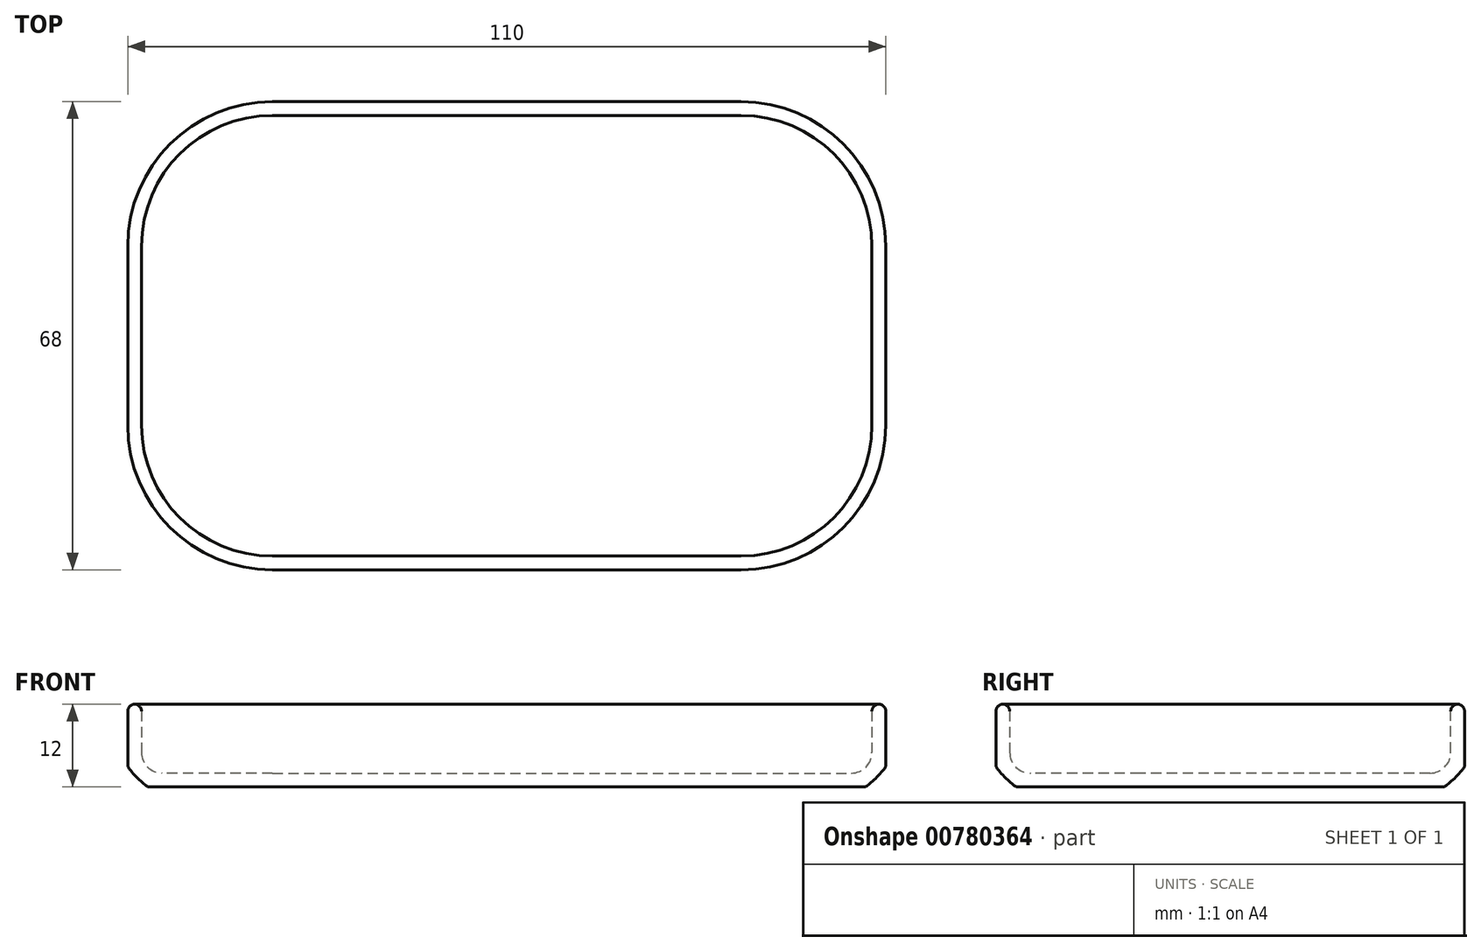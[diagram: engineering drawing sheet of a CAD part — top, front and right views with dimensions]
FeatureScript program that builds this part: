
annotation { "Feature Type Name" : "Feature", "Feature Type Description" : "" }
export const myFeature = defineFeature(function(context is Context, id is Id, definition is map)
    precondition{}
    {
        {
            var Q0;
            Q0=qCreatedBy(makeId("Top.planeOp"),FACE);
            var sketch = newSketch(context, id + "F0", { "sketchPlane" : qUnion([Q0])});
            skLineSegment(sketch, "E0", {"start": v(0, 34) * mm, "end": v(-34, 34) * mm});
            skLineSegment(sketch, "E1", {"start": v(-55, 13) * mm, "end": v(-55, 0) * mm});
            skPoint(sketch, "E2.visualSharp", {"position": v(-55, 34) * mm});
            skArc(sketch, "E2.filletArc", {"start": v(-34, 34) * mm, "mid": v(-48.85, 27.85) * mm, "end": v(-55, 13) * mm});
            skLineSegment(sketch, "E3.MirrorCS", {"start": v(0, 34) * mm, "end": v(34, 34) * mm});
            skLineSegment(sketch, "E4.MirrorCS", {"start": v(55, 13) * mm, "end": v(55, 0) * mm});
            skPoint(sketch, "E5.MirrorP", {"position": v(55, 34) * mm});
            skArc(sketch, "E6.MirrorCS", {"start": v(34, 34) * mm, "mid": v(48.85, 27.85) * mm, "end": v(55, 13) * mm});
            skLineSegment(sketch, "E7.MirrorCS", {"start": v(55, -13) * mm, "end": v(55, 0) * mm});
            skLineSegment(sketch, "E8.MirrorCS", {"start": v(-55, -13) * mm, "end": v(-55, 0) * mm});
            skLineSegment(sketch, "E9.MirrorCS", {"start": v(0, -34) * mm, "end": v(-34, -34) * mm});
            skLineSegment(sketch, "E10.MirrorCS", {"start": v(0, -34) * mm, "end": v(34, -34) * mm});
            skPoint(sketch, "E11.MirrorP", {"position": v(-55, -34) * mm});
            skPoint(sketch, "E12.MirrorP", {"position": v(55, -34) * mm});
            skArc(sketch, "E13.MirrorCS", {"start": v(34, -34) * mm, "mid": v(48.85, -27.85) * mm, "end": v(55, -13) * mm});
            skArc(sketch, "E14.MirrorCS", {"start": v(-34, -34) * mm, "mid": v(-48.85, -27.85) * mm, "end": v(-55, -13) * mm});
            skSolve(sketch);
        }
        {
            var Q0;
            Q0=qSketchRegion(id+"F0",true);
            extrude(context, id + "F1", {"entities" : qUnion([Q0]), "depth" : 12 * mm, "offsetDistance" : 25 * mm});
        }
        {
            var Q0;
            Q0=makeQuery(id+"F1.opExtrude","CAP_FACE",FACE,{"disambiguationData":[OSD([sQuery(id+"F0.wireOp",EDGE,"E1"),sQuery(id+"F0.wireOp",EDGE,"E0"),sQuery(id+"F0.wireOp",EDGE,"E2.filletArc"),sQuery(id+"F0.wireOp",EDGE,"E4.MirrorCS"),sQuery(id+"F0.wireOp",EDGE,"E3.MirrorCS"),sQuery(id+"F0.wireOp",EDGE,"E6.MirrorCS"),sQuery(id+"F0.wireOp",EDGE,"E10.MirrorCS"),sQuery(id+"F0.wireOp",EDGE,"E13.MirrorCS"),sQuery(id+"F0.wireOp",EDGE,"E7.MirrorCS"),sQuery(id+"F0.wireOp",EDGE,"E8.MirrorCS"),sQuery(id+"F0.wireOp",EDGE,"E9.MirrorCS"),sQuery(id+"F0.wireOp",EDGE,"E14.MirrorCS")])],"isStart":false});
            shell(context, id + "F2", {"entities" : qUnion([Q0]), "thickness" : 2 * mm});
        }
        {
            var Q0;
            Q0=makeQuery(id+"F2.opShell","OFFSET_FACE",FACE,{"disambiguationData":[OSD([sQuery(id+"F0.wireOp",EDGE,"E1"),sQuery(id+"F0.wireOp",EDGE,"E0"),sQuery(id+"F0.wireOp",EDGE,"E2.filletArc"),sQuery(id+"F0.wireOp",EDGE,"E4.MirrorCS"),sQuery(id+"F0.wireOp",EDGE,"E3.MirrorCS"),sQuery(id+"F0.wireOp",EDGE,"E6.MirrorCS"),sQuery(id+"F0.wireOp",EDGE,"E10.MirrorCS"),sQuery(id+"F0.wireOp",EDGE,"E13.MirrorCS"),sQuery(id+"F0.wireOp",EDGE,"E7.MirrorCS"),sQuery(id+"F0.wireOp",EDGE,"E8.MirrorCS"),sQuery(id+"F0.wireOp",EDGE,"E9.MirrorCS"),sQuery(id+"F0.wireOp",EDGE,"E14.MirrorCS")])]});
            fillet(context, id + "F3", {"entities" : qUnion([Q0]), "radius" : 3 * mm, "tangentPropagation" : true, "allowEdgeOverflow" : false});
        }
        {
            var Q0;
            Q0=makeQuery(id+"F1.opExtrude","CAP_FACE",FACE,{"disambiguationData":[OSD([sQuery(id+"F0.wireOp",EDGE,"E1"),sQuery(id+"F0.wireOp",EDGE,"E0"),sQuery(id+"F0.wireOp",EDGE,"E2.filletArc"),sQuery(id+"F0.wireOp",EDGE,"E4.MirrorCS"),sQuery(id+"F0.wireOp",EDGE,"E3.MirrorCS"),sQuery(id+"F0.wireOp",EDGE,"E6.MirrorCS"),sQuery(id+"F0.wireOp",EDGE,"E10.MirrorCS"),sQuery(id+"F0.wireOp",EDGE,"E13.MirrorCS"),sQuery(id+"F0.wireOp",EDGE,"E7.MirrorCS"),sQuery(id+"F0.wireOp",EDGE,"E8.MirrorCS"),sQuery(id+"F0.wireOp",EDGE,"E9.MirrorCS"),sQuery(id+"F0.wireOp",EDGE,"E14.MirrorCS")])],"isStart":false});
            fillet(context, id + "F4", {"entities" : qUnion([Q0]), "radius" : 1 * mm, "tangentPropagation" : true, "allowEdgeOverflow" : false});
        }
        {
            var Q0;
            Q0=makeQuery(id+"F1.opExtrude","CAP_FACE",FACE,{"disambiguationData":[OSD([sQuery(id+"F0.wireOp",EDGE,"E1"),sQuery(id+"F0.wireOp",EDGE,"E0"),sQuery(id+"F0.wireOp",EDGE,"E2.filletArc"),sQuery(id+"F0.wireOp",EDGE,"E4.MirrorCS"),sQuery(id+"F0.wireOp",EDGE,"E3.MirrorCS"),sQuery(id+"F0.wireOp",EDGE,"E6.MirrorCS"),sQuery(id+"F0.wireOp",EDGE,"E10.MirrorCS"),sQuery(id+"F0.wireOp",EDGE,"E13.MirrorCS"),sQuery(id+"F0.wireOp",EDGE,"E7.MirrorCS"),sQuery(id+"F0.wireOp",EDGE,"E8.MirrorCS"),sQuery(id+"F0.wireOp",EDGE,"E9.MirrorCS"),sQuery(id+"F0.wireOp",EDGE,"E14.MirrorCS")])],"isStart":true});
            fillet(context, id + "F5", {"entities" : qUnion([Q0]), "radius" : 3 * mm, "rho" : 0.1, "crossSection" : FilletCrossSection.CONIC, "allowEdgeOverflow" : false});
        }
    });
